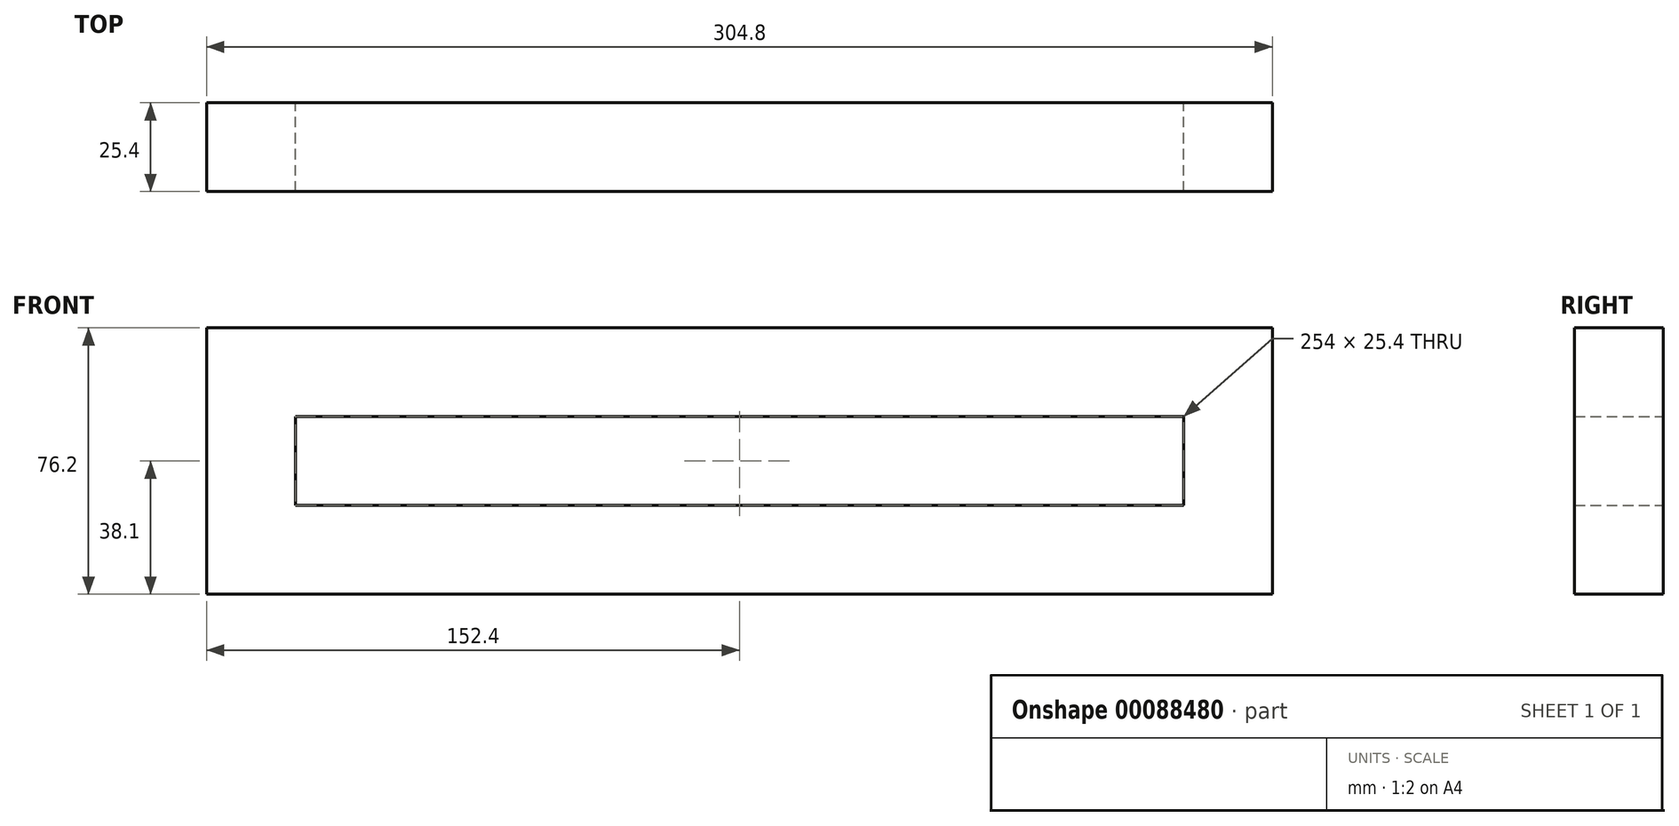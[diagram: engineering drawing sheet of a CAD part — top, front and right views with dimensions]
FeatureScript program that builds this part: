
annotation { "Feature Type Name" : "Feature", "Feature Type Description" : "" }
export const myFeature = defineFeature(function(context is Context, id is Id, definition is map)
    precondition{}
    {
        {
            var Q0;
            Q0=qCreatedBy(makeId("Front.planeOp"),FACE);
            var sketch = newSketch(context, id + "F0", { "sketchPlane" : qUnion([Q0])});
            skLineSegment(sketch, "E0.bottom", {"start": v(-152.4, 38.1) * mm, "end": v(152.4, 38.1) * mm});
            skLineSegment(sketch, "E0.top", {"start": v(-152.4, -38.1) * mm, "end": v(152.4, -38.1) * mm});
            skLineSegment(sketch, "E0.left", {"start": v(-152.4, 38.1) * mm, "end": v(-152.4, -38.1) * mm});
            skLineSegment(sketch, "E0.right", {"start": v(152.4, 38.1) * mm, "end": v(152.4, -38.1) * mm});
            skPoint(sketch, "E0.middle", {"position": v(0, 0) * mm});
            skLineSegment(sketch, "E1.0", {"start": v(-127, 12.7) * mm, "end": v(127, 12.7) * mm});
            skLineSegment(sketch, "E2.0", {"start": v(-127, -12.7) * mm, "end": v(127, -12.7) * mm});
            skLineSegment(sketch, "E3.0", {"start": v(-127, 12.7) * mm, "end": v(-127, -12.7) * mm});
            skLineSegment(sketch, "E4.0", {"start": v(127, 12.7) * mm, "end": v(127, -12.7) * mm});
            skSolve(sketch);
        }
        {
            var Q0;
            Q0=makeQuery(id+"F0.imprint","IMPRINT",FACE,{"disambiguationData":[TD([[makeQuery(id+"F0.imprint","IMPRINT",EDGE,{"derivedFrom":sQuery(id+"F0.wireOp",EDGE,"E0.bottom")}),-1.0]])]});
            extrude(context, id + "F1", {"entities" : qUnion([Q0]), "depth" : 25.4 * mm});
        }
    });
